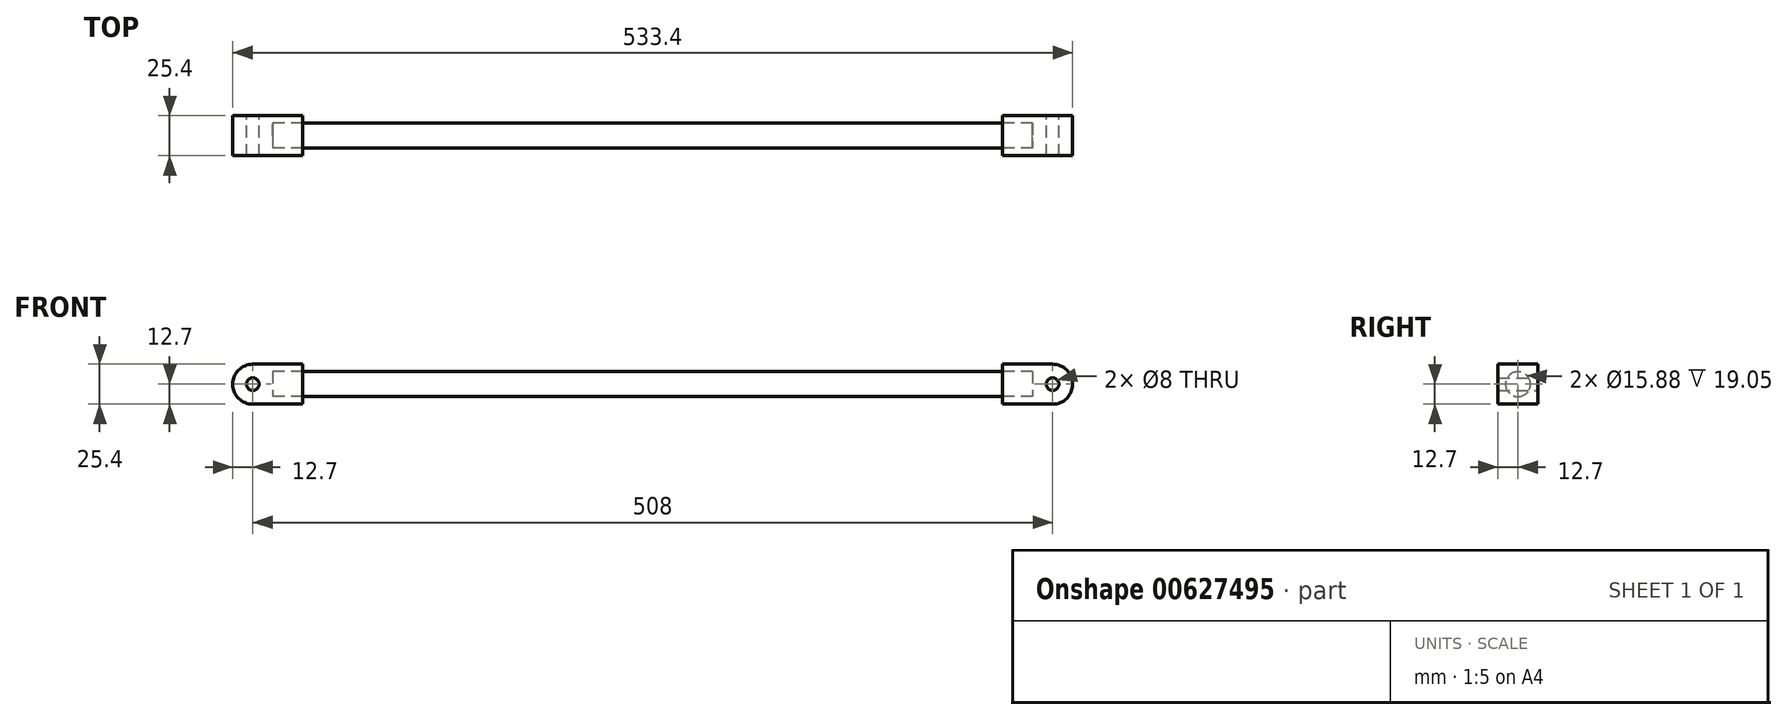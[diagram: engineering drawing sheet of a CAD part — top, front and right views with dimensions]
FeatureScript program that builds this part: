
annotation { "Feature Type Name" : "Feature", "Feature Type Description" : "" }
export const myFeature = defineFeature(function(context is Context, id is Id, definition is map)
    precondition{}
    {
        {
            var Q0;
            Q0=qCreatedBy(makeId("Front.planeOp"),FACE);
            var sketch = newSketch(context, id + "F0", { "sketchPlane" : qUnion([Q0])});
            skCircle(sketch, "E0", {"center": v(0, 0) * mm, "radius": 4 * mm});
            skArc(sketch, "E1", {"start": v(0, 12.7) * mm, "mid": v(12.7, 0) * mm, "end": v(0, -12.7) * mm});
            skLineSegment(sketch, "E2", {"start": v(0, 12.7) * mm, "end": v(-31.75, 12.7) * mm});
            skLineSegment(sketch, "E3", {"start": v(-31.75, 12.7) * mm, "end": v(-31.75, -12.7) * mm});
            skLineSegment(sketch, "E4", {"start": v(-31.75, -12.7) * mm, "end": v(0, -12.7) * mm});
            skSolve(sketch);
        }
        {
            var Q0;
            Q0 = qSketchRegion(id + "F0", true);
            extrude(context, id + "F1", {"entities" : qUnion([Q0]), "depth" : 25.4 * mm, "offsetDistance" : 25.4 * mm, "symmetric" : true});
        }
        {
            var Q0;
            Q0=makeQuery(id+"F1.opExtrude","SWEPT_FACE",FACE,{"disambiguationData":[OSD([sQuery(id+"F0.wireOp",EDGE,"E3")])]});
            var sketch = newSketch(context, id + "F2", { "sketchPlane" : qUnion([Q0])});
            skCircle(sketch, "E5", {"center": v(0, 0) * mm, "radius": 7.94 * mm});
            skSolve(sketch);
        }
        {
            var Q0;
            Q0 = qSketchRegion(id + "F2", true);
            extrude(context, id + "F3", {"entities" : qUnion([Q0]), "operationType" : NewBodyOperationType.REMOVE, "oppositeDirection" : true, "depth" : 19.05 * mm, "offsetDistance" : 25.4 * mm});
        }
        {
            var Q0;
            Q0=qCreatedBy(makeId("Right.planeOp"),FACE);
            cPlane(context, id + "F4", {"entities" : qUnion([Q0]), "cplaneType" : CPlaneType.OFFSET, "offset" : 254 * mm, "oppositeDirection" : true, "width" : 152.4 * mm, "height" : 152.4 * mm});
        }
        {
            var Q0;
            Q0=makeQuery(id+"F1.opExtrude","SWEPT_BODY",BODY,{"disambiguationData":[OSD([sQuery(id+"F0.wireOp",EDGE,"E0"),sQuery(id+"F0.wireOp",EDGE,"E1"),sQuery(id+"F0.wireOp",EDGE,"E2"),sQuery(id+"F0.wireOp",EDGE,"E3"),sQuery(id+"F0.wireOp",EDGE,"E4")])]});
            var Q1;
            Q1=qCreatedBy(id+"F4.planeOp",FACE);
            mirror(context, id + "F5", {"entities" : qUnion([Q0]), "mirrorPlane" : qUnion([Q1])});
        }
        {
            var Q0;
            Q0=qCreatedBy(id+"F4.planeOp",FACE);
            var sketch = newSketch(context, id + "F6", { "sketchPlane" : qUnion([Q0])});
            skCircle(sketch, "E6", {"center": v(0, 0) * mm, "radius": 7.94 * mm});
            skSolve(sketch);
        }
        {
            var Q0;
            Q0 = qSketchRegion(id + "F6", true);
            var Q1;
            Q1=makeQuery(id+"F3.boolean.opBoolean","COPY",FACE,{"derivedFrom":makeQuery(id+"F3.opExtrude","CAP_FACE",FACE,{"disambiguationData":[OSD([sQuery(id+"F2.wireOp",EDGE,"E5")])],"isStart":false})});
            var Q2;
            Q2=makeQuery(id+"F5.opPattern","COPY",FACE,{"derivedFrom":makeQuery(id+"F3.boolean.opBoolean","COPY",FACE,{"derivedFrom":makeQuery(id+"F3.opExtrude","CAP_FACE",FACE,{"disambiguationData":[OSD([sQuery(id+"F2.wireOp",EDGE,"E5")])],"isStart":false})}),"instanceName":"1"});
            extrude(context, id + "F7", {"entities" : qUnion([Q0]), "endBound" : BoundingType.UP_TO_SURFACE, "depth" : 25.4 * mm, "endBoundEntityFace" : qUnion([Q1]), "offsetDistance" : 25.4 * mm, "hasSecondDirection" : true, "secondDirectionBound" : BoundingType.UP_TO_SURFACE, "secondDirectionOppositeDirection" : true, "secondDirectionDepth" : 25.4 * mm, "secondDirectionBoundEntityFace" : qUnion([Q2])});
        }
    });
